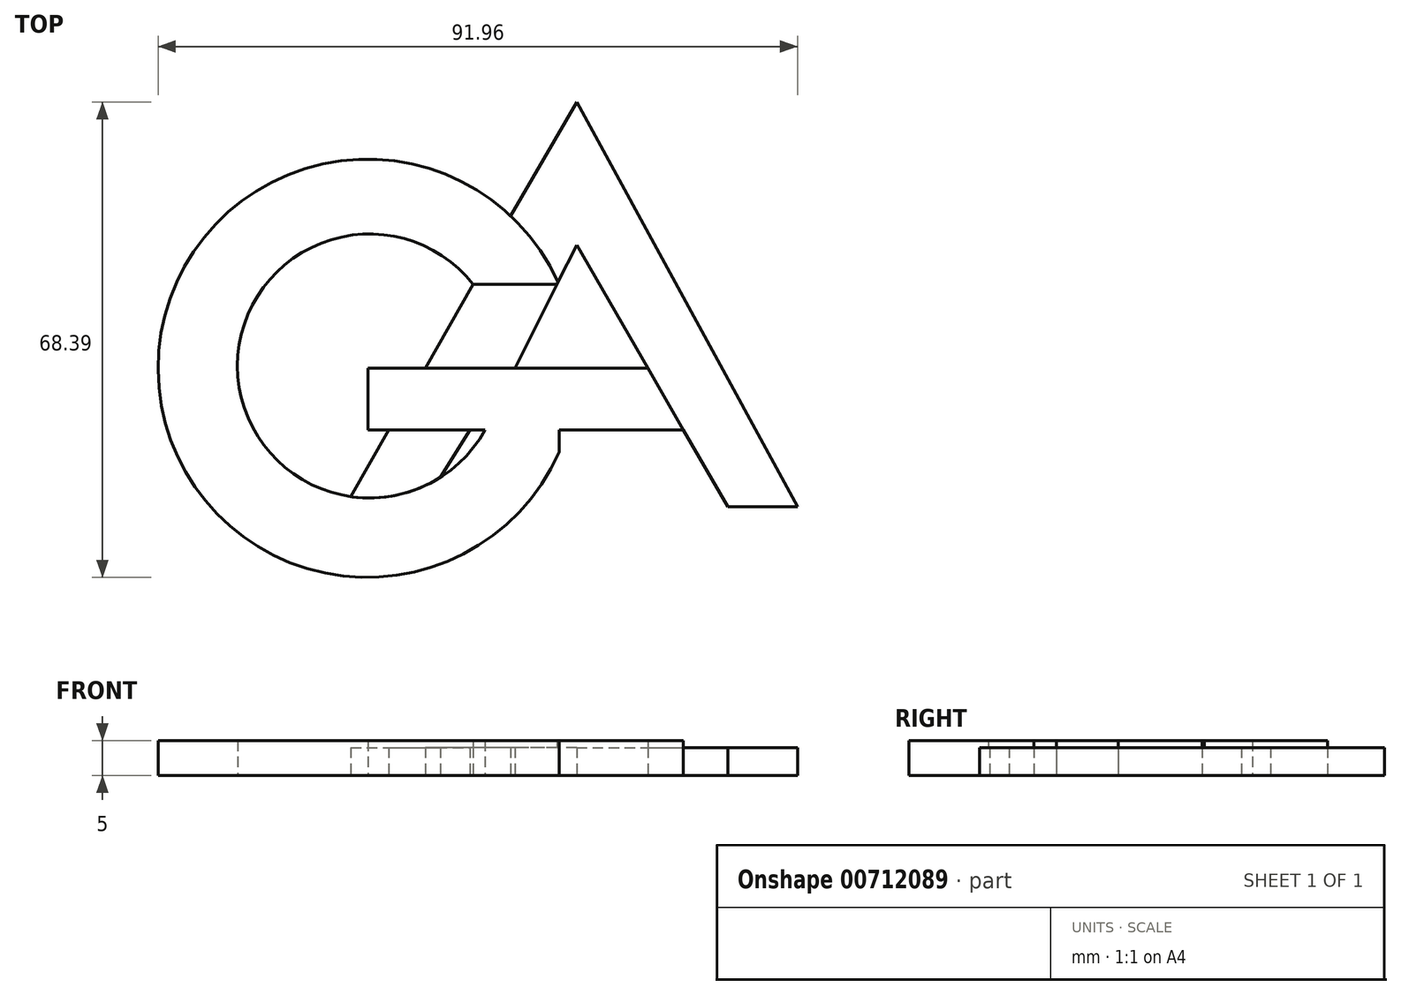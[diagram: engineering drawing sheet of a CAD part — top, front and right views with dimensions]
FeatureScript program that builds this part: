
annotation { "Feature Type Name" : "Feature", "Feature Type Description" : "" }
export const myFeature = defineFeature(function(context is Context, id is Id, definition is map)
    precondition{}
    {
        {
            var Q0;
            Q0=qCreatedBy(makeId("Top.planeOp"),FACE);
            var sketch = newSketch(context, id + "F0", { "sketchPlane" : qUnion([Q0])});
            skLineSegment(sketch, "E0", {"start": v(0, 0) * mm, "end": v(-30, 0) * mm});
            skLineSegment(sketch, "E1", {"start": v(0, 0) * mm, "end": v(0, 0) * mm});
            skLineSegment(sketch, "E2.2", {"start": v(0, 38.3) * mm, "end": v(31.77, -19.94) * mm});
            skLineSegment(sketch, "E3.bottom", {"start": v(-30, 0) * mm, "end": v(0, 0) * mm});
            skLineSegment(sketch, "E3.left", {"start": v(-30, 0) * mm, "end": v(-30, -8.86) * mm});
            skLineSegment(sketch, "E4", {"start": v(-2.54, 12.08) * mm, "end": v(-14.86, 12.08) * mm});
            skLineSegment(sketch, "E5", {"start": v(-14.86, 12.08) * mm, "end": v(-2.54, 12.08) * mm});
            skLineSegment(sketch, "E6", {"start": v(-30, -8.86) * mm, "end": v(-13.16, -8.86) * mm});
            skLineSegment(sketch, "E7", {"start": v(0, 38.3) * mm, "end": v(-9.48, 21.88) * mm});
            skArc(sketch, "E8", {"start": v(-14.86, 12.08) * mm, "mid": v(-48.7, -1.21) * mm, "end": v(-13.16, -8.86) * mm});
            skArc(sketch, "E9", {"start": v(-2.54, 12.08) * mm, "mid": v(-60.2, 0) * mm, "end": v(-2.54, -12.08) * mm});
            skLineSegment(sketch, "E10", {"start": v(-2.54, -12.08) * mm, "end": v(-2.54, -8.86) * mm});
            skLineSegment(sketch, "E11", {"start": v(-2.54, -8.86) * mm, "end": v(0, -8.86) * mm});
            skLineSegment(sketch, "E12", {"start": v(-32.47, -18.47) * mm, "end": v(-27.01, -8.86) * mm});
            skLineSegment(sketch, "E13", {"start": v(-14.86, 12.08) * mm, "end": v(-21.77, 0) * mm});
            skLineSegment(sketch, "E14.2", {"start": v(0, 17.72) * mm, "end": v(15.35, -8.86) * mm});
            skLineSegment(sketch, "E15", {"start": v(10.23, 0) * mm, "end": v(0, 0) * mm});
            skLineSegment(sketch, "E16", {"start": v(-8.86, 0) * mm, "end": v(10.23, 0) * mm});
            skLineSegment(sketch, "E17", {"start": v(15.35, -8.86) * mm, "end": v(21.74, -19.94) * mm});
            skLineSegment(sketch, "E18", {"start": v(-15.35, -8.86) * mm, "end": v(-19.58, -15.7) * mm});
            skLineSegment(sketch, "E19", {"start": v(21.74, -19.94) * mm, "end": v(31.77, -19.94) * mm});
            skLineSegment(sketch, "E20", {"start": v(0, -8.86) * mm, "end": v(15.35, -8.86) * mm});
            skLineSegment(sketch, "E21", {"start": v(0, 17.72) * mm, "end": v(-8.86, 0) * mm});
            skSolve(sketch);
        }
        {
            var Q0;
            {var subQ12=sQuery(id+"F0.wireOp",EDGE,"E3.left");Q0=makeQuery(id+"F0.imprint","IMPRINT",FACE,{"disambiguationData":[TD([[makeQuery(id+"F0.imprint","IMPRINT",EDGE,{"derivedFrom":subQ12}),1.0]])]});}
            extrude(context, id + "F1", {"entities" : qUnion([Q0]), "depth" : 5 * mm, "offsetDistance" : 25 * mm});
        }
        {
            var Q0;
            {var subQ0=sQuery(id+"F0.wireOp",EDGE,"E12");Q0=makeQuery(id+"F0.imprint","IMPRINT",FACE,{"disambiguationData":[TD([[makeQuery(id+"F0.imprint","IMPRINT",EDGE,{"derivedFrom":subQ0}),-1.0]])]});}
            var Q1;
            {var subQ3=sQuery(id+"F0.wireOp",EDGE,"E13");Q1=makeQuery(id+"F0.imprint","IMPRINT",FACE,{"disambiguationData":[TD([[makeQuery(id+"F0.imprint","IMPRINT",EDGE,{"derivedFrom":subQ3}),1.0]])]});}
            var Q2;
            {var subQ5=sQuery(id+"F0.wireOp",EDGE,"E2.2");Q2=makeQuery(id+"F0.imprint","IMPRINT",FACE,{"disambiguationData":[TD([[makeQuery(id+"F0.imprint","IMPRINT",EDGE,{"derivedFrom":subQ5}),-1.0]])]});}
            extrude(context, id + "F2", {"entities" : qUnion([Q0, Q1, Q2]), "operationType" : NewBodyOperationType.ADD, "depth" : 4 * mm, "offsetDistance" : 25 * mm});
        }
    });
